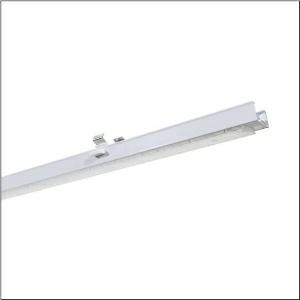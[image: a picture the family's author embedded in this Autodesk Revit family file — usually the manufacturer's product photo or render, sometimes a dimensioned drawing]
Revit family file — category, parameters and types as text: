
# Revit family: trunking_flex_31_51re18mb1cb
name_source: partatom
category: Lighting Fixtures
units: mm (PartAtom-declared; Revit-internal decimal feet)

## family parameters
Cut with Voids When Loaded = No
Host = Face
Light Source = No
Part Type = Normal
Room Calculation Point = No
Round Connector Dimension = Use Diameter
Shared = No

## types (1)
- --- (1 x LED, 11500 lm, 66 W, 3500K)
    Apparent Load = 66 VA
    CIE Flux Codes = 71 89 97 97 100
    Color Rendering = 80
    Color Temperature = 3500K
    Default Elevation = 1800 mm
    Description = Trunking Flex 31, luminaire insert, of extruded aluminium section, coated, traffic white (RAL 9016), length: 1.472mm, width: 91mm, height: 53mm, LED rated luminous flux: 11.500lm, light colour: 835, control gear: ON/OFF Multilumen, with system connector: socket, mains connection: 220..240V, AC, 50/60Hz, rated input power: 66W, luminous flux adjustable on luminaire in eight steps (3450/4380/5800/6700/8350/9200/10500/11500lm ), connected load according to luminous flux setting (19/24/32/37/47/52/60/66W), primary light control with lens, of plastic, primary optical cover: cover, of PMMA, light emission: direct distribution, protection rating (complete): IP20, insulation class (complete): insulation class I (protective earthing), certification: CE, UKCA, impact resistance: IK02, permissible ambient temperature for indoor applications: -20..+40°C, packaging unit: 1 piece
    Height = 58 mm
    Lamp = 1 x LED
    Lamp Light Flux = 11500 lm
    Lamp Power = 66 W
    Lamp count = 1
    Length = 1472 mm
    Luminous efficacy = 174 lm/W
    Manufacturer = Siteco
    ModVariant = No
    Model = 51RE18MB1CB
    Mounting Place = Ceiling
    Mounting Type = Pendant
    Number of Poles = 1
    OnlyDefault = Yes
    Power Factor = 1
    Product Name = Trunking Flex 31
    Product group = luminaire insert
    ProductGroupID = 902
    Protection Class = Protection class I
    Protection Degree = IP 20
    RLX_Detail_Level = 1
    RLX_Emergency_Light_Flux = 0 lm
    RLX_Emergency_Type = 0
    RLX_Emergency_Type_DB = No
    RlxData = <blob elided: 21089 chars, md5=de51af91>
    Socket = socket
    Standby Power = 0 W
    System Light Flux = 11500 lm
    System Power = 66 W
    Type Comments = factory setting: luminous flux: 100 % | (ON | ON | ON)
    Type Image = l_1266702.jpg
    URL = http://relux.com
    VarID = @adj_059086
    Voltage = 0 V
    Weight = 0.00 kg
    Width = 65 mm

## geometry (parser evidence)
native form markers: Blend x4, Sweep x10
no freeform markers — native parametric forms only
